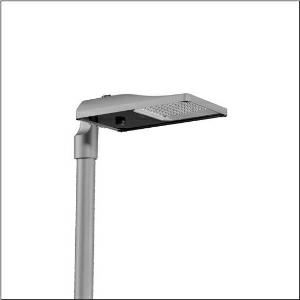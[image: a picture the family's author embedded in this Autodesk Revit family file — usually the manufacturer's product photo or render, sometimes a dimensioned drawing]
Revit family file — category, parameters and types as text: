
# Revit family: streetlight_sl_31_midi___st0_5a_5xh7b31t08la_752d
name_source: partatom
category: Lighting Fixtures
units: mm (PartAtom-declared; Revit-internal decimal feet)

## family parameters
Cut with Voids When Loaded = No
Host = Face
Light Source = No
Part Type = Normal
Room Calculation Point = No
Round Connector Dimension = Use Diameter
Shared = No

## types (1)
- --- (1 x LED, 13170 lm, 86.5 W, 3000K)
    Apparent Load = 87 VA
    CIE Flux Codes = 41 75 97 100 100
    Color Rendering = 70
    Color Temperature = 3000K
    Default Elevation = 1800 mm
    Description = Streetlight SL 31 midi D4i, Desk-Remote mast luminaire for post-top, side-entry; light control with lens of PMMA; light distribution: ST0.5a, direct asymmetric distribution, for standard-compliant lighting for roads and squares; LED: luminous flux: 13.170lm, light colour: 730, colour temperature: 3000K; luminous efficacy: 152,3lm/W; control: pre-setting: logarithmic dimming characteristic, flexible luminous flux parameterisation, time-dependent luminous flux control, constant luminous flux control, power reduction, intelligent temperature release in ECG and LED module, overheat protection; luminaire housing, of diecast aluminium, Siteco® metallic grey (DB 702S), corrosivity category C5 high according to DIN EN ISO 12944; cover of toughened safety glass, transparent, opened without tools; mast flange of diecast aluminium, Siteco® metallic grey (DB 702S), spigot size: 76/60mm, mast flange included unmounted; with cable H07RN-F 2x 1.5mm², cable length: 10,5m, connection cable pre-assembled; mains connection: 220..240V, AC, 50/60Hz; power consumption (at start of service life): 86,5W / (at end of service life): 90W / (with reduced operation 50%): 39,6W; protection rating (complete): IP66; insulation class (complete): insulation class II (safety insulation); impact resistance: IK09; certification: CE, ENEC, ENEC+, VDE, UKCA, ZD4i; permissible operating ambient temperature for outdoor applications: -40..+50°C; packaging unit: 1 piece

Light Distribution: ST0.5a
    Height = 79 mm
    Lamp = 1 x LED
    Lamp Light Flux = 13170 lm
    Lamp Power = 86.5 W
    Lamp count = 1
    Length = 577 mm
    Luminous efficacy = 152 lm/W
    Manufacturer = Siteco
    ModVariant = No
    Model = 5XH7B31T08LA
    Number of Poles = 1
    OnlyDefault = Yes
    Power Factor = 1
    Product Name = Streetlight SL 31 midi | ST0.5a
    Product group = mast luminaire | pylon top
    ProductGroupID = 6100
    Protection Class = Protection class II
    Protection Degree = IP 66
    RLX_Detail_Level = 1
    RLX_Emergency_Light_Flux = 0 lm
    RLX_Emergency_Type = 0
    RLX_Emergency_Type_DB = No
    RlxData = <blob elided: 53617 chars, md5=61a7b001>
    Socket = socket
    Standby Power = 0 W
    System Light Flux = 13170 lm
    System Power = 87 W
    Type Comments = factory setting: luminous flux: 100 % | dim-lin: 254 | 456 mA
    Type Image = l_1300321.jpg
    URL = http://relux.com
    VarID = @adj_078145
    Voltage = 0 V
    Weight = 0.00 kg
    Width = 362 mm

## geometry (parser evidence)
native form markers: Blend x4, Sweep x11
no freeform markers — native parametric forms only
